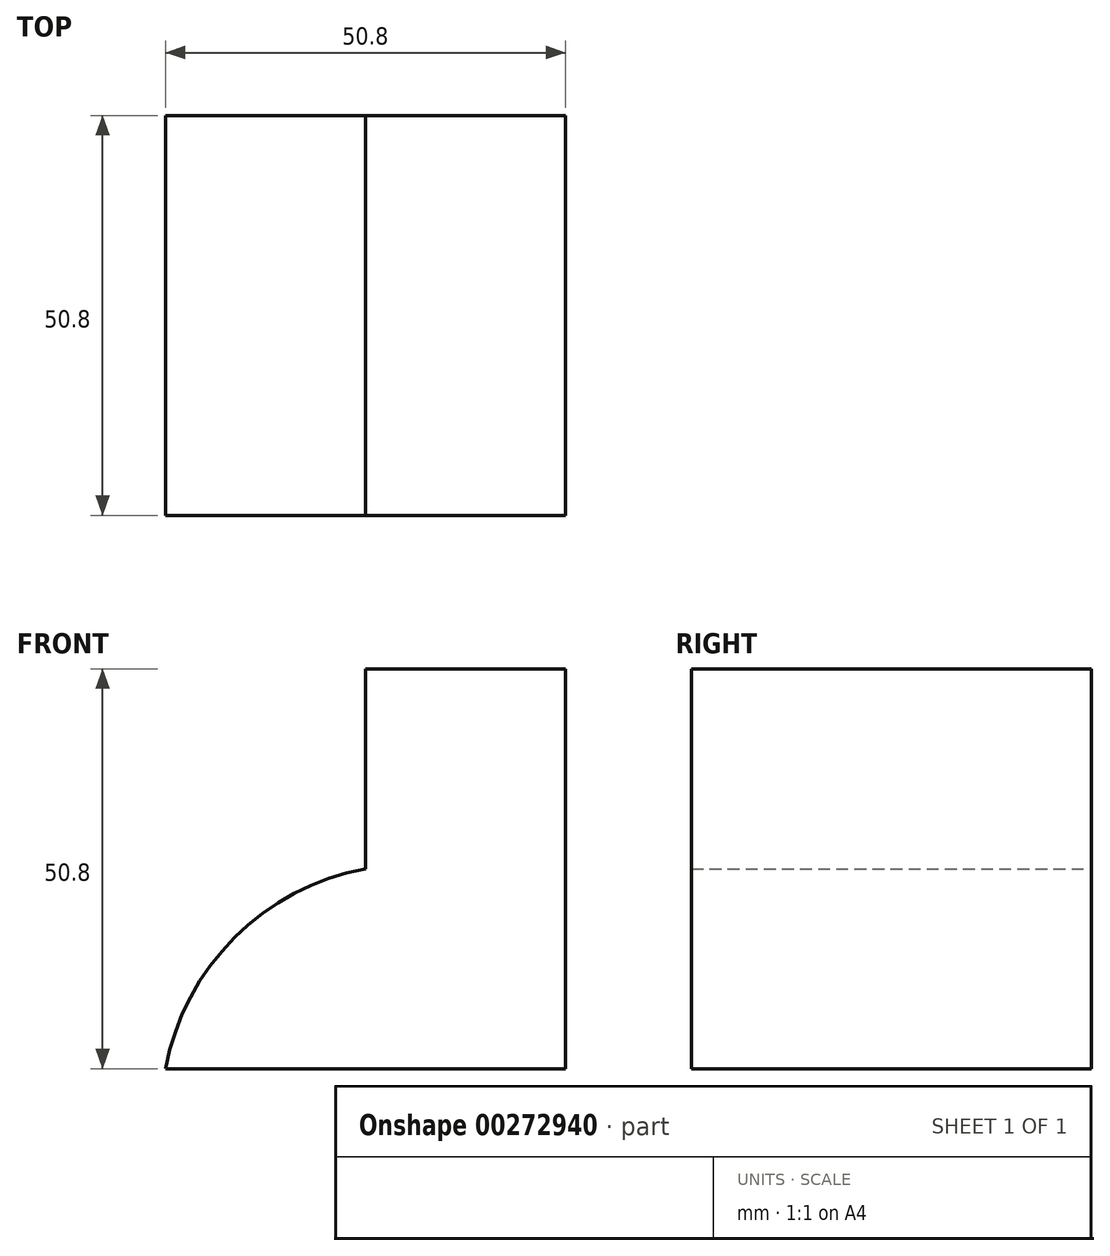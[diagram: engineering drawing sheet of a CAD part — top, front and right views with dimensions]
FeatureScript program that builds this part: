
annotation { "Feature Type Name" : "Feature", "Feature Type Description" : "" }
export const myFeature = defineFeature(function(context is Context, id is Id, definition is map)
    precondition{}
    {
        {
            var Q0;
            Q0=qCreatedBy(makeId("Front.planeOp"),FACE);
            var sketch = newSketch(context, id + "F0", { "sketchPlane" : qUnion([Q0])});
            skLineSegment(sketch, "E0", {"start": v(-23.48, 16.42) * mm, "end": v(-23.48, 41.82) * mm});
            skLineSegment(sketch, "E1", {"start": v(-23.48, 41.82) * mm, "end": v(1.92, 41.82) * mm});
            skLineSegment(sketch, "E2", {"start": v(1.92, 41.82) * mm, "end": v(1.92, -8.98) * mm});
            skLineSegment(sketch, "E3", {"start": v(1.92, -8.98) * mm, "end": v(-48.88, -8.98) * mm});
            skArc(sketch, "E4", {"start": v(-23.48, 16.42) * mm, "mid": v(-40.13, 7.67) * mm, "end": v(-48.88, -8.98) * mm});
            skSolve(sketch);
        }
        {
            var Q0;
            Q0 = qSketchRegion(id + "F0", true);
            extrude(context, id + "F1", {"entities" : qUnion([Q0]), "depth" : 50.8 * mm});
        }
    });
